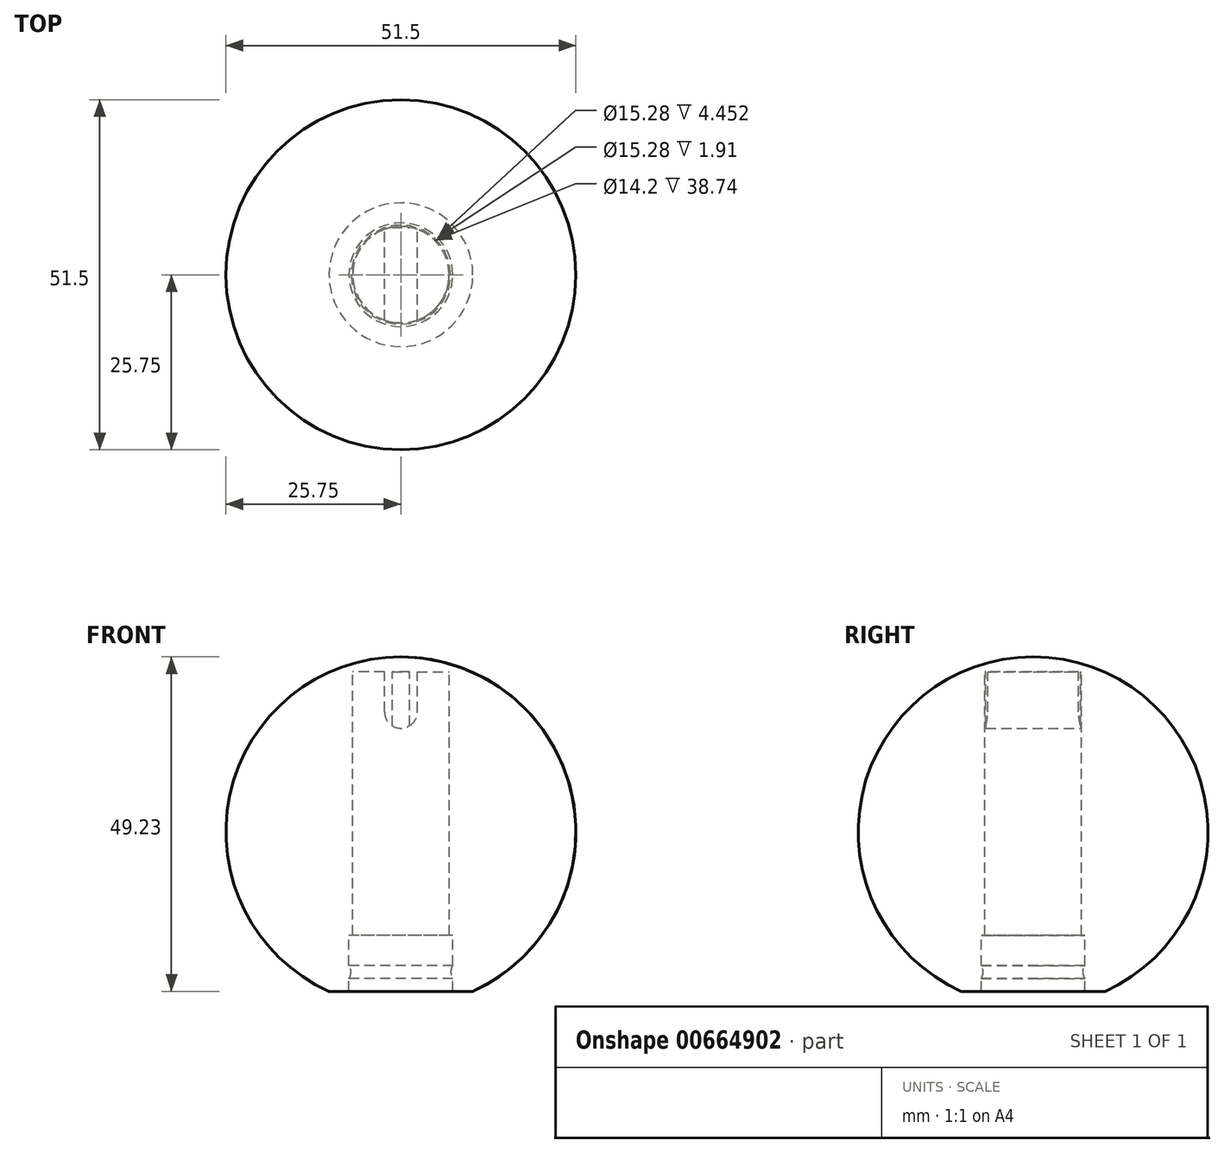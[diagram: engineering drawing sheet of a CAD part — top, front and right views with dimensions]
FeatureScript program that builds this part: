
annotation { "Feature Type Name" : "Feature", "Feature Type Description" : "" }
export const myFeature = defineFeature(function(context is Context, id is Id, definition is map)
    precondition{}
    {
        {
            var Q0;
            Q0=qCreatedBy(makeId("Front.planeOp"),FACE);
            var sketch = newSketch(context, id + "F0", { "sketchPlane" : qUnion([Q0])});
            skLineSegment(sketch, "E0", {"start": v(0, 0) * mm, "end": v(7.1, 0) * mm});
            skLineSegment(sketch, "E1", {"start": v(7.1, 0) * mm, "end": v(7.1, -38.74) * mm});
            skLineSegment(sketch, "E2", {"start": v(7.64, -47) * mm, "end": v(10.58, -47) * mm});
            skLineSegment(sketch, "E3", {"start": v(7.64, -38.74) * mm, "end": v(7.1, -38.74) * mm});
            skLineSegment(sketch, "E4", {"start": v(0, 0) * mm, "end": v(2.4, 0) * mm});
            skLineSegment(sketch, "E5", {"start": v(2.4, 0) * mm, "end": v(2.4, -5.88) * mm});
            skLineSegment(sketch, "E6", {"start": v(2.4, -5.88) * mm, "end": v(0, -5.88) * mm});
            skLineSegment(sketch, "E7", {"start": v(0, -5.88) * mm, "end": v(-2.4, -5.88) * mm});
            skLineSegment(sketch, "E8", {"start": v(-2.4, -5.88) * mm, "end": v(-2.4, 0) * mm});
            skLineSegment(sketch, "E9", {"start": v(-2.4, 0) * mm, "end": v(0, 0) * mm});
            skArc(sketch, "E10", {"start": v(2.4, -5.88) * mm, "mid": v(0, -8.28) * mm, "end": v(-2.4, -5.88) * mm});
            skLineSegment(sketch, "E11", {"start": v(7.64, -47) * mm, "end": v(7.64, -44.14) * mm});
            skLineSegment(sketch, "E12", {"start": v(7.64, -44.14) * mm, "end": v(7.64, -38.74) * mm});
            skLineSegment(sketch, "E13", {"start": v(7.64, -44.14) * mm, "end": v(7.34, -44.14) * mm});
            skLineSegment(sketch, "E14", {"start": v(7.64, -44.14) * mm, "end": v(7.64, -43.2) * mm});
            skLineSegment(sketch, "E15", {"start": v(7.64, -44.14) * mm, "end": v(7.64, -45.1) * mm});
            skArc(sketch, "E16", {"start": v(7.64, -43.2) * mm, "mid": v(7.34, -44.14) * mm, "end": v(7.64, -45.1) * mm});
            skArc(sketch, "E17", {"start": v(10.58, -47) * mm, "mid": v(25.18, -18.11) * mm, "end": v(0, 2.23) * mm});
            skLineSegment(sketch, "E18", {"start": v(0, 2.23) * mm, "end": v(0, 0) * mm});
            skSolve(sketch);
        }
        {
            var Q0;
            {var subQ0=sQuery(id+"F0.wireOp",EDGE,"E5");Q0=makeQuery(id+"F0.imprint","IMPRINT",FACE,{"disambiguationData":[TD([[makeQuery(id+"F0.imprint","IMPRINT",EDGE,{"derivedFrom":subQ0}),-1.0]])]});}
            var Q1;
            Q1=makeQuery(id+"F0.imprint","IMPRINT",FACE,{"disambiguationData":[TD([[makeQuery(id+"F0.imprint","IMPRINT",EDGE,{"derivedFrom":sQuery(id+"F0.wireOp",EDGE,"E6")}),1.0]])]});
            extrude(context, id + "F1", {"entities" : qUnion([Q0, Q1]), "endBound" : BoundingType.SYMMETRIC, "depth" : 13.97 * mm, "offsetDistance" : 25.4 * mm});
        }
        {
            var Q0;
            {var subQ7=sQuery(id+"F0.wireOp",EDGE,"E1");Q0=makeQuery(id+"F0.imprint","IMPRINT",FACE,{"disambiguationData":[TD([[makeQuery(id+"F0.imprint","IMPRINT",EDGE,{"derivedFrom":subQ7}),1.0]])]});}
            var Q1;
            {var subQ0=sQuery(id+"F0.wireOp",EDGE,"E13");Q1=makeQuery(id+"F0.imprint","IMPRINT",FACE,{"disambiguationData":[TD([[makeQuery(id+"F0.imprint","IMPRINT",EDGE,{"derivedFrom":subQ0}),-1.0]])]});}
            var Q2;
            {var subQ0=sQuery(id+"F0.wireOp",EDGE,"E13");Q2=makeQuery(id+"F0.imprint","IMPRINT",FACE,{"disambiguationData":[TD([[makeQuery(id+"F0.imprint","IMPRINT",EDGE,{"derivedFrom":subQ0}),1.0]])]});}
            var Q3;
            Q3=sQuery(id+"F0.wireOp",EDGE,"E18");
            revolve(context, id + "F2", {"operationType" : NewBodyOperationType.ADD, "entities" : qUnion([Q0, Q1, Q2]), "axis" : qUnion([Q3]), "revolveType" : RevolveType.FULL, "surfaceOperationType" : NewSurfaceOperationType.NEW});
        }
    });
